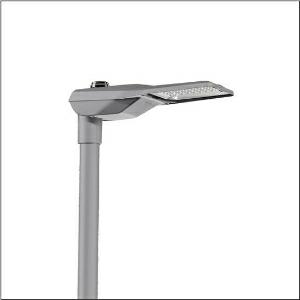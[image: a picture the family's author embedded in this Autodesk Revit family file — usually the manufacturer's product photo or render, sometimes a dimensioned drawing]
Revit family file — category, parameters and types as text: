
# Revit family: streetlight_sl_21_mini___st1_0a_5xe6d67n08jb_11ba
name_source: partatom
category: Lighting Fixtures
units: mm (PartAtom-declared; Revit-internal decimal feet)

## family parameters
Cut with Voids When Loaded = No
Host = Face
Light Source = No
Part Type = Normal
Room Calculation Point = No
Round Connector Dimension = Use Diameter
Shared = No

## types (1)
- --- (1 x LED, 11500 lm, 87.3 W, 2700K)
    Apparent Load = 87 VA
    CIE Flux Codes = 40 73 97 100 100
    Color Rendering = 70
    Color Temperature = 2700K
    Default Elevation = 1800 mm
    Description = Streetlight SL 21 mini, mast luminaire, primary light control with lens, of PMMA, primary optical cover: cover, of toughened safety glass, transparent, light distribution: ST1.0a, light emission: direct distribution, primary light characteristic: asymmetric, installation type: side-entry, LED, 3G 2.5mm², High Power LED, rated luminous flux: 11.500lm, luminous efficacy: 132lm/W, light colour: 727, colour temperature: 2700K, control gear: NEMA (7pin), control: overheat protection, pre-setting: linear dimming characteristic, constant luminous flux control, time-dependent luminous flux control, flexible luminous flux parameterisation, mains connection: 230..240V, AC, 50/60Hz, connection cable pre-assembled, cable length: 10,5m, wiring characteristics: H05VV-F, start of lifetime: 87W, end of service life: 90W, reduction: 40W, luminaire housing, of diecast aluminium (EN AC-44300), powder-coated, Siteco® metallic grey (DB 702S), corrosivity category C5 mid according to DIN EN ISO 12944, multi-level sealing system, sealing non-destructively replaceable, inclination adjustable: 0°, 5°, 10°, 15°, length: 628mm, width: 235mm, height: 110mm, spigot size: 42mm (side-entry), mounting height: 4..8m, protection rating (complete): IP66, insulation class (complete): insulation class I (protective earthing), certification: CE, ENEC, ENEC+, VDE, impact resistance: IK10, permissible operating ambient temperature for outdoor applications: -40..+50°C, standard-compliant lighting for roads and squares, packaging unit: 1 piece

Light Distribution: ST1.0a
    Height = 110 mm
    Lamp = 1 x LED
    Lamp Light Flux = 11500 lm
    Lamp Power = 87.3 W
    Lamp count = 1
    Length = 625 mm
    Luminous efficacy = 132 lm/W
    Manufacturer = Siteco
    ModVariant = No
    Model = 5XE6D67N08JB
    Number of Poles = 1
    OnlyDefault = Yes
    Power Factor = 1
    Product Name = Streetlight SL 21 mini | ST1.0a
    Product group = mast luminaire | pylon top
    ProductGroupID = 6100
    Protection Class = Protection class I
    Protection Degree = IP 66
    RLX_Detail_Level = 1
    RLX_Emergency_Light_Flux = 0 lm
    RLX_Emergency_Type = 0
    RLX_Emergency_Type_DB = No
    RlxData = <blob elided: 26085 chars, md5=0102b65b>
    Socket = socket
    Standby Power = 0 W
    System Light Flux = 11500 lm
    System Power = 87 W
    Type Comments = factory setting: luminous flux: 100 % | dim-lin: 254 | 915 mA
    Type Image = l_1294379.jpg
    URL = http://relux.com
    VarID = @adj_156721
    Voltage = 0 V
    Weight = 0.00 kg
    Width = 234 mm

## geometry (parser evidence)
native form markers: Blend x4, Sweep x10
no freeform markers — native parametric forms only
